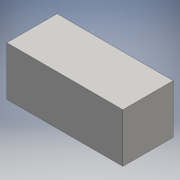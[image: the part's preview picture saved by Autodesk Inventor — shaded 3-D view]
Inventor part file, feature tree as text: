
AUTODESK INVENTOR PART (.ipt)
format: ipt  version: 2016 (Build 200138000, 138)  size: 97,280 bytes
history: native  units: mm
features: extrude x2, sketch x2, other x1
ambient origin geometry x8: Origin, YZ Plane, XZ Plane, XY Plane, X Axis, Y Axis, Z Axis, Center Point
bodies: Body1 (feature_tree)
feature tree (5):
  other  "Sólido1"
  extrude  "Extrusión1"  Depth=19.0mm TaperAngle=0.0deg
  extrude  "Extrusión2"  [1 undecoded]
  sketch  "Boceto1"  dims[d7=19.5mm d8=0.0mm d17=19.0mm d18=0.0mm]
  sketch  "Boceto2"
note: 1 required parameter value undecoded (feature->parameter linkage not recoverable at this tier; creation-order binding heuristic only, values carry confidence <= 0.55)
